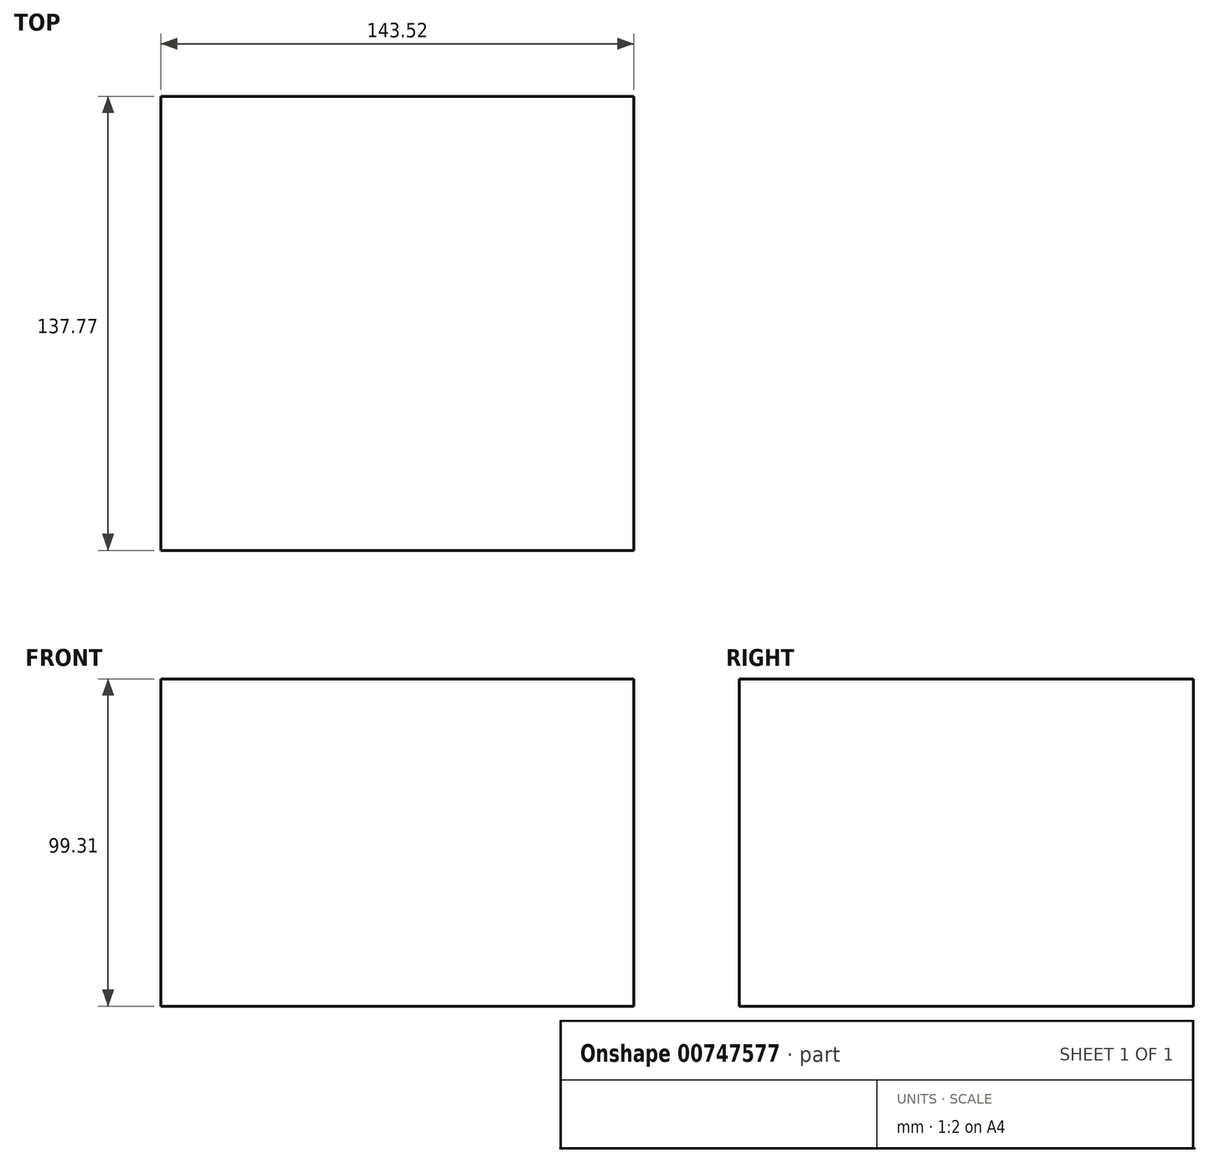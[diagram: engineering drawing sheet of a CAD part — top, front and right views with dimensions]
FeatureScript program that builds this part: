
annotation { "Feature Type Name" : "Feature", "Feature Type Description" : "" }
export const myFeature = defineFeature(function(context is Context, id is Id, definition is map)
    precondition{}
    {
        {
            var Q0;
            Q0=qCreatedBy(makeId("Top.planeOp"),FACE);
            var sketch = newSketch(context, id + "F0", { "sketchPlane" : qUnion([Q0])});
            skLineSegment(sketch, "E0.bottom", {"start": v(0, 0) * mm, "end": v(143.52, 0) * mm});
            skLineSegment(sketch, "E0.top", {"start": v(0, 137.77) * mm, "end": v(143.52, 137.77) * mm});
            skLineSegment(sketch, "E0.left", {"start": v(0, 0) * mm, "end": v(0, 137.77) * mm});
            skLineSegment(sketch, "E0.right", {"start": v(143.52, 0) * mm, "end": v(143.52, 137.77) * mm});
            skSolve(sketch);
        }
        {
            var Q0;
            Q0 = qSketchRegion(id + "F0", true);
            extrude(context, id + "F1", {"entities" : qUnion([Q0]), "depth" : 99.31 * mm, "offsetDistance" : 25.4 * mm});
        }
    });
